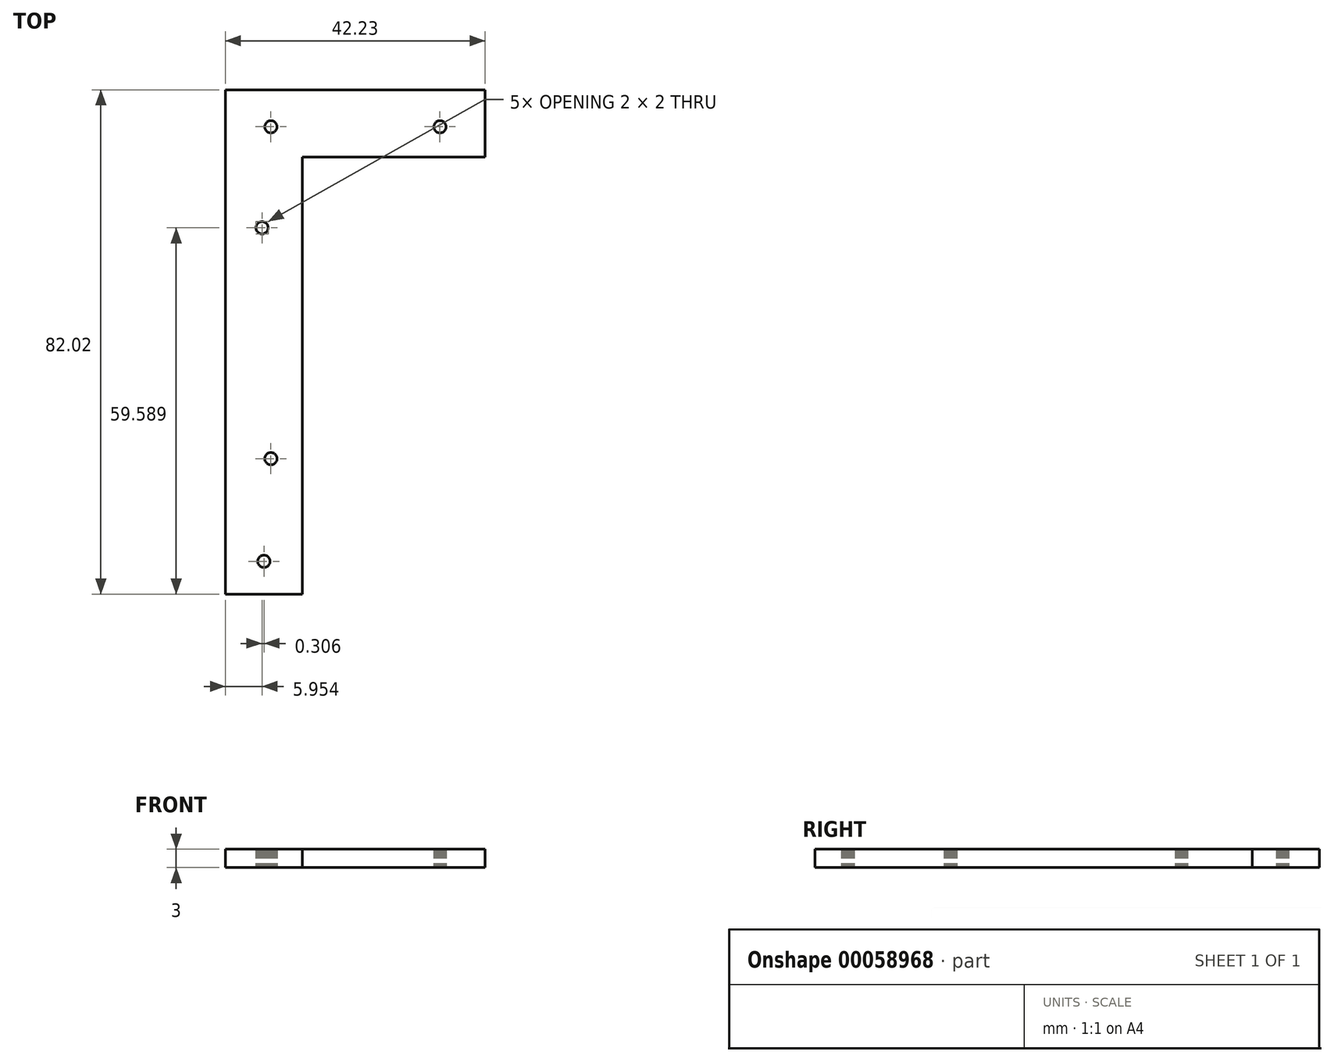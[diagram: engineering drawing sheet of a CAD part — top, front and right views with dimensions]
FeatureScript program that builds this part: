
annotation { "Feature Type Name" : "Feature", "Feature Type Description" : "" }
export const myFeature = defineFeature(function(context is Context, id is Id, definition is map)
    precondition{}
    {
        {
            var Q0;
            Q0=qCreatedBy(makeId("Top.planeOp"),FACE);
            var sketch = newSketch(context, id + "F0", { "sketchPlane" : qUnion([Q0])});
            skLineSegment(sketch, "E0", {"start": v(0.84, 33.8) * mm, "end": v(0.83, 33.92) * mm});
            skLineSegment(sketch, "E1", {"start": v(0.83, 33.92) * mm, "end": v(0.81, 34.04) * mm});
            skLineSegment(sketch, "E2", {"start": v(0.81, 34.04) * mm, "end": v(0.77, 34.16) * mm});
            skLineSegment(sketch, "E3", {"start": v(0.77, 34.16) * mm, "end": v(0.72, 34.28) * mm});
            skLineSegment(sketch, "E4", {"start": v(0.72, 34.28) * mm, "end": v(0.65, 34.38) * mm});
            skLineSegment(sketch, "E5", {"start": v(0.65, 34.38) * mm, "end": v(0.57, 34.48) * mm});
            skLineSegment(sketch, "E6", {"start": v(0.57, 34.48) * mm, "end": v(0.48, 34.57) * mm});
            skLineSegment(sketch, "E7", {"start": v(0.48, 34.57) * mm, "end": v(0.38, 34.64) * mm});
            skLineSegment(sketch, "E8", {"start": v(0.38, 34.64) * mm, "end": v(0.27, 34.7) * mm});
            skLineSegment(sketch, "E9", {"start": v(0.27, 34.7) * mm, "end": v(0.15, 34.75) * mm});
            skLineSegment(sketch, "E10", {"start": v(0.15, 34.75) * mm, "end": v(0.03, 34.78) * mm});
            skLineSegment(sketch, "E11", {"start": v(0.03, 34.78) * mm, "end": v(-0.1, 34.8) * mm});
            skLineSegment(sketch, "E12", {"start": v(-0.1, 34.8) * mm, "end": v(-0.22, 34.8) * mm});
            skLineSegment(sketch, "E13", {"start": v(-0.22, 34.8) * mm, "end": v(-0.35, 34.78) * mm});
            skLineSegment(sketch, "E14", {"start": v(-0.35, 34.78) * mm, "end": v(-0.47, 34.75) * mm});
            skLineSegment(sketch, "E15", {"start": v(-2.64, 34.75) * mm, "end": v(-2.76, 34.7) * mm});
            skLineSegment(sketch, "E16", {"start": v(-0.58, 34.7) * mm, "end": v(-0.7, 34.64) * mm});
            skLineSegment(sketch, "E17", {"start": v(-0.7, 34.64) * mm, "end": v(-0.8, 34.57) * mm});
            skLineSegment(sketch, "E18", {"start": v(-0.8, 34.57) * mm, "end": v(-0.89, 34.48) * mm});
            skLineSegment(sketch, "E19", {"start": v(-0.89, 34.48) * mm, "end": v(-0.97, 34.38) * mm});
            skLineSegment(sketch, "E20", {"start": v(-0.97, 34.38) * mm, "end": v(-1.03, 34.28) * mm});
            skLineSegment(sketch, "E21", {"start": v(-1.03, 34.28) * mm, "end": v(-1.09, 34.16) * mm});
            skLineSegment(sketch, "E22", {"start": v(-1.09, 34.16) * mm, "end": v(-1.13, 34.04) * mm});
            skLineSegment(sketch, "E23", {"start": v(-1.13, 34.04) * mm, "end": v(-1.15, 33.92) * mm});
            skLineSegment(sketch, "E24", {"start": v(-1.15, 33.92) * mm, "end": v(-1.16, 33.8) * mm});
            skLineSegment(sketch, "E25", {"start": v(-1.16, 33.8) * mm, "end": v(-1.15, 33.67) * mm});
            skLineSegment(sketch, "E26", {"start": v(-1.15, 33.67) * mm, "end": v(-1.13, 33.55) * mm});
            skLineSegment(sketch, "E27", {"start": v(-1.13, 33.55) * mm, "end": v(-1.09, 33.43) * mm});
            skLineSegment(sketch, "E28", {"start": v(-1.09, 33.43) * mm, "end": v(-1.03, 33.31) * mm});
            skLineSegment(sketch, "E29", {"start": v(-1.03, 33.31) * mm, "end": v(-0.97, 33.2) * mm});
            skLineSegment(sketch, "E30", {"start": v(-0.97, 33.2) * mm, "end": v(-0.89, 33.11) * mm});
            skLineSegment(sketch, "E31", {"start": v(-0.89, 33.11) * mm, "end": v(-0.8, 33.03) * mm});
            skLineSegment(sketch, "E32", {"start": v(-0.8, 33.03) * mm, "end": v(-0.7, 32.95) * mm});
            skLineSegment(sketch, "E33", {"start": v(-0.7, 32.95) * mm, "end": v(-0.58, 32.9) * mm});
            skLineSegment(sketch, "E34", {"start": v(-0.58, 32.9) * mm, "end": v(-0.47, 32.85) * mm});
            skLineSegment(sketch, "E35", {"start": v(-0.47, 32.85) * mm, "end": v(-0.35, 32.81) * mm});
            skLineSegment(sketch, "E36", {"start": v(-0.35, 32.81) * mm, "end": v(-0.22, 32.8) * mm});
            skLineSegment(sketch, "E37", {"start": v(-0.22, 32.8) * mm, "end": v(-0.1, 32.8) * mm});
            skLineSegment(sketch, "E38", {"start": v(-0.1, 32.8) * mm, "end": v(0.03, 32.81) * mm});
            skLineSegment(sketch, "E39", {"start": v(0.03, 32.81) * mm, "end": v(0.15, 32.85) * mm});
            skLineSegment(sketch, "E40", {"start": v(0.15, 32.85) * mm, "end": v(0.27, 32.9) * mm});
            skLineSegment(sketch, "E41", {"start": v(0.27, 32.9) * mm, "end": v(0.38, 32.95) * mm});
            skLineSegment(sketch, "E42", {"start": v(0.38, 32.95) * mm, "end": v(0.48, 33.03) * mm});
            skLineSegment(sketch, "E43", {"start": v(0.48, 33.03) * mm, "end": v(0.57, 33.11) * mm});
            skLineSegment(sketch, "E44", {"start": v(0.57, 33.11) * mm, "end": v(0.65, 33.2) * mm});
            skLineSegment(sketch, "E45", {"start": v(0.65, 33.2) * mm, "end": v(0.72, 33.31) * mm});
            skLineSegment(sketch, "E46", {"start": v(0.72, 33.31) * mm, "end": v(0.77, 33.43) * mm});
            skLineSegment(sketch, "E47", {"start": v(0.77, 33.43) * mm, "end": v(0.81, 33.55) * mm});
            skLineSegment(sketch, "E48", {"start": v(0.81, 33.55) * mm, "end": v(0.83, 33.67) * mm});
            skLineSegment(sketch, "E49", {"start": v(0.83, 33.67) * mm, "end": v(0.84, 33.8) * mm});
            skLineSegment(sketch, "E50", {"start": v(-0.29, -36.9) * mm, "end": v(-0.3, -36.78) * mm});
            skLineSegment(sketch, "E51", {"start": v(-0.3, -36.78) * mm, "end": v(-0.32, -36.66) * mm});
            skLineSegment(sketch, "E52", {"start": v(-0.32, -36.66) * mm, "end": v(-0.36, -36.54) * mm});
            skLineSegment(sketch, "E53", {"start": v(-0.36, -36.54) * mm, "end": v(-0.41, -36.42) * mm});
            skLineSegment(sketch, "E54", {"start": v(-0.41, -36.42) * mm, "end": v(-0.48, -36.32) * mm});
            skLineSegment(sketch, "E55", {"start": v(-0.48, -36.32) * mm, "end": v(-0.56, -36.22) * mm});
            skLineSegment(sketch, "E56", {"start": v(-0.56, -36.22) * mm, "end": v(-0.65, -36.14) * mm});
            skLineSegment(sketch, "E57", {"start": v(-0.65, -36.14) * mm, "end": v(-0.75, -36.06) * mm});
            skLineSegment(sketch, "E58", {"start": v(-0.75, -36.06) * mm, "end": v(-0.86, -36) * mm});
            skLineSegment(sketch, "E59", {"start": v(-0.86, -36) * mm, "end": v(-0.98, -35.95) * mm});
            skLineSegment(sketch, "E60", {"start": v(-0.98, -35.95) * mm, "end": v(-1.1, -35.92) * mm});
            skLineSegment(sketch, "E61", {"start": v(-1.1, -35.92) * mm, "end": v(-1.23, -35.9) * mm});
            skLineSegment(sketch, "E62", {"start": v(-1.23, -35.9) * mm, "end": v(-1.35, -35.9) * mm});
            skLineSegment(sketch, "E63", {"start": v(-1.35, -35.9) * mm, "end": v(-1.48, -35.92) * mm});
            skLineSegment(sketch, "E64", {"start": v(-1.48, -35.92) * mm, "end": v(-1.6, -35.95) * mm});
            skLineSegment(sketch, "E65", {"start": v(-1.6, -35.95) * mm, "end": v(-1.72, -36) * mm});
            skLineSegment(sketch, "E66", {"start": v(-1.72, -36) * mm, "end": v(-1.83, -36.06) * mm});
            skLineSegment(sketch, "E67", {"start": v(-1.83, -36.06) * mm, "end": v(-1.93, -36.14) * mm});
            skLineSegment(sketch, "E68", {"start": v(-1.93, -36.14) * mm, "end": v(-2.02, -36.22) * mm});
            skLineSegment(sketch, "E69", {"start": v(-2.02, -36.22) * mm, "end": v(-2.1, -36.32) * mm});
            skLineSegment(sketch, "E70", {"start": v(-2.1, -36.32) * mm, "end": v(-2.17, -36.42) * mm});
            skLineSegment(sketch, "E71", {"start": v(-2.17, -36.42) * mm, "end": v(-2.22, -36.54) * mm});
            skLineSegment(sketch, "E72", {"start": v(-2.22, -36.54) * mm, "end": v(-2.26, -36.66) * mm});
            skLineSegment(sketch, "E73", {"start": v(-2.26, -36.66) * mm, "end": v(-2.28, -36.78) * mm});
            skLineSegment(sketch, "E74", {"start": v(-2.28, -36.78) * mm, "end": v(-2.29, -36.9) * mm});
            skLineSegment(sketch, "E75", {"start": v(-2.29, -36.9) * mm, "end": v(-2.28, -37.03) * mm});
            skLineSegment(sketch, "E76", {"start": v(-2.28, -37.03) * mm, "end": v(-2.26, -37.15) * mm});
            skLineSegment(sketch, "E77", {"start": v(-2.26, -37.15) * mm, "end": v(-2.22, -37.27) * mm});
            skLineSegment(sketch, "E78", {"start": v(-2.22, -37.27) * mm, "end": v(-2.17, -37.39) * mm});
            skLineSegment(sketch, "E79", {"start": v(-2.17, -37.39) * mm, "end": v(-2.1, -37.5) * mm});
            skLineSegment(sketch, "E80", {"start": v(-2.1, -37.5) * mm, "end": v(-2.02, -37.6) * mm});
            skLineSegment(sketch, "E81", {"start": v(-2.02, -37.6) * mm, "end": v(-1.93, -37.68) * mm});
            skLineSegment(sketch, "E82", {"start": v(-1.93, -37.68) * mm, "end": v(-1.83, -37.75) * mm});
            skLineSegment(sketch, "E83", {"start": v(-1.83, -37.75) * mm, "end": v(-1.72, -37.81) * mm});
            skLineSegment(sketch, "E84", {"start": v(-1.72, -37.81) * mm, "end": v(-1.6, -37.86) * mm});
            skLineSegment(sketch, "E85", {"start": v(-1.6, -37.86) * mm, "end": v(-1.48, -37.89) * mm});
            skLineSegment(sketch, "E86", {"start": v(-1.48, -37.89) * mm, "end": v(-1.35, -37.9) * mm});
            skLineSegment(sketch, "E87", {"start": v(-1.35, -37.9) * mm, "end": v(-1.23, -37.9) * mm});
            skLineSegment(sketch, "E88", {"start": v(-1.23, -37.9) * mm, "end": v(-1.1, -37.89) * mm});
            skLineSegment(sketch, "E89", {"start": v(-1.1, -37.89) * mm, "end": v(-0.98, -37.86) * mm});
            skLineSegment(sketch, "E90", {"start": v(-0.98, -37.86) * mm, "end": v(-0.86, -37.81) * mm});
            skLineSegment(sketch, "E91", {"start": v(-0.86, -37.81) * mm, "end": v(-0.75, -37.75) * mm});
            skLineSegment(sketch, "E92", {"start": v(-0.75, -37.75) * mm, "end": v(-0.65, -37.68) * mm});
            skLineSegment(sketch, "E93", {"start": v(-0.65, -37.68) * mm, "end": v(-0.56, -37.6) * mm});
            skLineSegment(sketch, "E94", {"start": v(-0.56, -37.6) * mm, "end": v(-0.48, -37.5) * mm});
            skLineSegment(sketch, "E95", {"start": v(-0.48, -37.5) * mm, "end": v(-0.41, -37.39) * mm});
            skLineSegment(sketch, "E96", {"start": v(-0.41, -37.39) * mm, "end": v(-0.36, -37.27) * mm});
            skLineSegment(sketch, "E97", {"start": v(-0.36, -37.27) * mm, "end": v(-0.32, -37.15) * mm});
            skLineSegment(sketch, "E98", {"start": v(-0.32, -37.15) * mm, "end": v(-0.3, -37.03) * mm});
            skLineSegment(sketch, "E99", {"start": v(-0.3, -37.03) * mm, "end": v(-0.29, -36.9) * mm});
            skLineSegment(sketch, "E100", {"start": v(-0.6, 17.36) * mm, "end": v(-0.6, 17.48) * mm});
            skLineSegment(sketch, "E101", {"start": v(-0.6, 17.48) * mm, "end": v(-0.63, 17.6) * mm});
            skLineSegment(sketch, "E102", {"start": v(-0.63, 17.6) * mm, "end": v(-0.67, 17.73) * mm});
            skLineSegment(sketch, "E103", {"start": v(-0.67, 17.73) * mm, "end": v(-0.72, 17.84) * mm});
            skLineSegment(sketch, "E104", {"start": v(-0.72, 17.84) * mm, "end": v(-0.79, 17.95) * mm});
            skLineSegment(sketch, "E105", {"start": v(-0.79, 17.95) * mm, "end": v(-0.87, 18.04) * mm});
            skLineSegment(sketch, "E106", {"start": v(-0.87, 18.04) * mm, "end": v(-0.96, 18.13) * mm});
            skLineSegment(sketch, "E107", {"start": v(-0.96, 18.13) * mm, "end": v(-1.06, 18.2) * mm});
            skLineSegment(sketch, "E108", {"start": v(-1.06, 18.2) * mm, "end": v(-1.17, 18.26) * mm});
            skLineSegment(sketch, "E109", {"start": v(-1.17, 18.26) * mm, "end": v(-1.29, 18.3) * mm});
            skLineSegment(sketch, "E110", {"start": v(-1.29, 18.3) * mm, "end": v(-1.4, 18.34) * mm});
            skLineSegment(sketch, "E111", {"start": v(-1.4, 18.34) * mm, "end": v(-1.53, 18.36) * mm});
            skLineSegment(sketch, "E112", {"start": v(-1.53, 18.36) * mm, "end": v(-1.66, 18.36) * mm});
            skLineSegment(sketch, "E113", {"start": v(-1.66, 18.36) * mm, "end": v(-1.78, 18.34) * mm});
            skLineSegment(sketch, "E114", {"start": v(-1.78, 18.34) * mm, "end": v(-1.9, 18.3) * mm});
            skLineSegment(sketch, "E115", {"start": v(-1.9, 18.3) * mm, "end": v(-2.02, 18.26) * mm});
            skLineSegment(sketch, "E116", {"start": v(-2.02, 18.26) * mm, "end": v(-2.13, 18.2) * mm});
            skLineSegment(sketch, "E117", {"start": v(-2.13, 18.2) * mm, "end": v(-2.23, 18.13) * mm});
            skLineSegment(sketch, "E118", {"start": v(-2.23, 18.13) * mm, "end": v(-2.32, 18.04) * mm});
            skLineSegment(sketch, "E119", {"start": v(-2.32, 18.04) * mm, "end": v(-2.4, 17.95) * mm});
            skLineSegment(sketch, "E120", {"start": v(-2.4, 17.95) * mm, "end": v(-2.47, 17.84) * mm});
            skLineSegment(sketch, "E121", {"start": v(-2.47, 17.84) * mm, "end": v(-2.53, 17.73) * mm});
            skLineSegment(sketch, "E122", {"start": v(-2.53, 17.73) * mm, "end": v(-2.56, 17.6) * mm});
            skLineSegment(sketch, "E123", {"start": v(-2.56, 17.6) * mm, "end": v(-2.59, 17.48) * mm});
            skLineSegment(sketch, "E124", {"start": v(-2.59, 17.48) * mm, "end": v(-2.6, 17.36) * mm});
            skLineSegment(sketch, "E125", {"start": v(-2.6, 17.36) * mm, "end": v(-2.59, 17.23) * mm});
            skLineSegment(sketch, "E126", {"start": v(-2.59, 17.23) * mm, "end": v(-2.56, 17.11) * mm});
            skLineSegment(sketch, "E127", {"start": v(-2.56, 17.11) * mm, "end": v(-2.53, 17) * mm});
            skLineSegment(sketch, "E128", {"start": v(-2.53, 17) * mm, "end": v(-2.47, 16.88) * mm});
            skLineSegment(sketch, "E129", {"start": v(-2.47, 16.88) * mm, "end": v(-2.4, 16.77) * mm});
            skLineSegment(sketch, "E130", {"start": v(-2.4, 16.77) * mm, "end": v(-2.32, 16.67) * mm});
            skLineSegment(sketch, "E131", {"start": v(-2.32, 16.67) * mm, "end": v(-2.23, 16.59) * mm});
            skLineSegment(sketch, "E132", {"start": v(-2.23, 16.59) * mm, "end": v(-2.13, 16.51) * mm});
            skLineSegment(sketch, "E133", {"start": v(-2.13, 16.51) * mm, "end": v(-2.02, 16.45) * mm});
            skLineSegment(sketch, "E134", {"start": v(-2.02, 16.45) * mm, "end": v(-1.9, 16.4) * mm});
            skLineSegment(sketch, "E135", {"start": v(-1.9, 16.4) * mm, "end": v(-1.78, 16.38) * mm});
            skLineSegment(sketch, "E136", {"start": v(-1.78, 16.38) * mm, "end": v(-1.66, 16.36) * mm});
            skLineSegment(sketch, "E137", {"start": v(-1.66, 16.36) * mm, "end": v(-1.53, 16.36) * mm});
            skLineSegment(sketch, "E138", {"start": v(-1.53, 16.36) * mm, "end": v(-1.4, 16.38) * mm});
            skLineSegment(sketch, "E139", {"start": v(-1.4, 16.38) * mm, "end": v(-1.29, 16.4) * mm});
            skLineSegment(sketch, "E140", {"start": v(-1.29, 16.4) * mm, "end": v(-1.17, 16.45) * mm});
            skLineSegment(sketch, "E141", {"start": v(-1.17, 16.45) * mm, "end": v(-1.06, 16.51) * mm});
            skLineSegment(sketch, "E142", {"start": v(-1.06, 16.51) * mm, "end": v(-0.96, 16.59) * mm});
            skLineSegment(sketch, "E143", {"start": v(-0.96, 16.59) * mm, "end": v(-0.87, 16.67) * mm});
            skLineSegment(sketch, "E144", {"start": v(-0.87, 16.67) * mm, "end": v(-0.79, 16.77) * mm});
            skLineSegment(sketch, "E145", {"start": v(-0.79, 16.77) * mm, "end": v(-0.72, 16.88) * mm});
            skLineSegment(sketch, "E146", {"start": v(-0.72, 16.88) * mm, "end": v(-0.67, 17) * mm});
            skLineSegment(sketch, "E147", {"start": v(-0.67, 17) * mm, "end": v(-0.63, 17.11) * mm});
            skLineSegment(sketch, "E148", {"start": v(-0.63, 17.11) * mm, "end": v(-0.6, 17.23) * mm});
            skLineSegment(sketch, "E149", {"start": v(-0.6, 17.23) * mm, "end": v(-0.6, 17.36) * mm});
            skLineSegment(sketch, "E150", {"start": v(0.84, -20.2) * mm, "end": v(0.83, -20.08) * mm});
            skLineSegment(sketch, "E151", {"start": v(0.83, -20.08) * mm, "end": v(0.81, -19.96) * mm});
            skLineSegment(sketch, "E152", {"start": v(0.81, -19.96) * mm, "end": v(0.77, -19.84) * mm});
            skLineSegment(sketch, "E153", {"start": v(0.77, -19.84) * mm, "end": v(0.72, -19.72) * mm});
            skLineSegment(sketch, "E154", {"start": v(0.72, -19.72) * mm, "end": v(0.65, -19.62) * mm});
            skLineSegment(sketch, "E155", {"start": v(0.65, -19.62) * mm, "end": v(0.57, -19.52) * mm});
            skLineSegment(sketch, "E156", {"start": v(0.57, -19.52) * mm, "end": v(0.48, -19.43) * mm});
            skLineSegment(sketch, "E157", {"start": v(0.48, -19.43) * mm, "end": v(0.38, -19.36) * mm});
            skLineSegment(sketch, "E158", {"start": v(0.38, -19.36) * mm, "end": v(0.27, -19.3) * mm});
            skLineSegment(sketch, "E159", {"start": v(0.27, -19.3) * mm, "end": v(0.15, -19.25) * mm});
            skLineSegment(sketch, "E160", {"start": v(0.15, -19.25) * mm, "end": v(0.03, -19.22) * mm});
            skLineSegment(sketch, "E161", {"start": v(0.03, -19.22) * mm, "end": v(-0.1, -19.2) * mm});
            skLineSegment(sketch, "E162", {"start": v(-0.1, -19.2) * mm, "end": v(-0.22, -19.2) * mm});
            skLineSegment(sketch, "E163", {"start": v(-0.22, -19.2) * mm, "end": v(-0.35, -19.22) * mm});
            skLineSegment(sketch, "E164", {"start": v(-0.35, -19.22) * mm, "end": v(-0.47, -19.25) * mm});
            skLineSegment(sketch, "E165", {"start": v(-0.47, -19.25) * mm, "end": v(-0.58, -19.3) * mm});
            skLineSegment(sketch, "E166", {"start": v(-0.58, -19.3) * mm, "end": v(-0.7, -19.36) * mm});
            skLineSegment(sketch, "E167", {"start": v(-0.7, -19.36) * mm, "end": v(-0.8, -19.43) * mm});
            skLineSegment(sketch, "E168", {"start": v(-0.8, -19.43) * mm, "end": v(-0.89, -19.52) * mm});
            skLineSegment(sketch, "E169", {"start": v(-0.89, -19.52) * mm, "end": v(-0.97, -19.62) * mm});
            skLineSegment(sketch, "E170", {"start": v(-0.97, -19.62) * mm, "end": v(-1.03, -19.72) * mm});
            skLineSegment(sketch, "E171", {"start": v(-1.03, -19.72) * mm, "end": v(-1.09, -19.84) * mm});
            skLineSegment(sketch, "E172", {"start": v(-1.09, -19.84) * mm, "end": v(-1.13, -19.96) * mm});
            skLineSegment(sketch, "E173", {"start": v(-1.13, -19.96) * mm, "end": v(-1.15, -20.08) * mm});
            skLineSegment(sketch, "E174", {"start": v(-1.15, -20.08) * mm, "end": v(-1.16, -20.2) * mm});
            skLineSegment(sketch, "E175", {"start": v(-1.16, -20.2) * mm, "end": v(-1.15, -20.33) * mm});
            skLineSegment(sketch, "E176", {"start": v(-1.15, -20.33) * mm, "end": v(-1.13, -20.45) * mm});
            skLineSegment(sketch, "E177", {"start": v(-1.13, -20.45) * mm, "end": v(-1.09, -20.57) * mm});
            skLineSegment(sketch, "E178", {"start": v(-1.09, -20.57) * mm, "end": v(-1.03, -20.69) * mm});
            skLineSegment(sketch, "E179", {"start": v(-1.03, -20.69) * mm, "end": v(-0.97, -20.8) * mm});
            skLineSegment(sketch, "E180", {"start": v(-0.97, -20.8) * mm, "end": v(-0.89, -20.89) * mm});
            skLineSegment(sketch, "E181", {"start": v(-0.89, -20.89) * mm, "end": v(-0.8, -20.97) * mm});
            skLineSegment(sketch, "E182", {"start": v(-0.8, -20.97) * mm, "end": v(-0.7, -21.05) * mm});
            skLineSegment(sketch, "E183", {"start": v(-0.7, -21.05) * mm, "end": v(-0.58, -21.1) * mm});
            skLineSegment(sketch, "E184", {"start": v(-0.58, -21.1) * mm, "end": v(-0.47, -21.15) * mm});
            skLineSegment(sketch, "E185", {"start": v(-0.47, -21.15) * mm, "end": v(-0.35, -21.19) * mm});
            skLineSegment(sketch, "E186", {"start": v(-0.35, -21.19) * mm, "end": v(-0.22, -21.2) * mm});
            skLineSegment(sketch, "E187", {"start": v(-0.22, -21.2) * mm, "end": v(-0.1, -21.2) * mm});
            skLineSegment(sketch, "E188", {"start": v(-0.1, -21.2) * mm, "end": v(0.03, -21.19) * mm});
            skLineSegment(sketch, "E189", {"start": v(0.03, -21.19) * mm, "end": v(0.15, -21.15) * mm});
            skLineSegment(sketch, "E190", {"start": v(0.15, -21.15) * mm, "end": v(0.27, -21.1) * mm});
            skLineSegment(sketch, "E191", {"start": v(0.27, -21.1) * mm, "end": v(0.38, -21.05) * mm});
            skLineSegment(sketch, "E192", {"start": v(0.38, -21.05) * mm, "end": v(0.48, -20.97) * mm});
            skLineSegment(sketch, "E193", {"start": v(0.48, -20.97) * mm, "end": v(0.57, -20.89) * mm});
            skLineSegment(sketch, "E194", {"start": v(0.57, -20.89) * mm, "end": v(0.65, -20.8) * mm});
            skLineSegment(sketch, "E195", {"start": v(0.65, -20.8) * mm, "end": v(0.72, -20.69) * mm});
            skLineSegment(sketch, "E196", {"start": v(0.72, -20.69) * mm, "end": v(0.77, -20.57) * mm});
            skLineSegment(sketch, "E197", {"start": v(0.77, -20.57) * mm, "end": v(0.81, -20.45) * mm});
            skLineSegment(sketch, "E198", {"start": v(0.81, -20.45) * mm, "end": v(0.83, -20.33) * mm});
            skLineSegment(sketch, "E199", {"start": v(0.83, -20.33) * mm, "end": v(0.84, -20.2) * mm});
            skLineSegment(sketch, "E200", {"start": v(-0.47, 34.75) * mm, "end": v(-0.58, 34.7) * mm});
            skLineSegment(sketch, "E201", {"start": v(28.34, 33.8) * mm, "end": v(28.33, 33.92) * mm});
            skLineSegment(sketch, "E202", {"start": v(28.33, 33.92) * mm, "end": v(28.31, 34.04) * mm});
            skLineSegment(sketch, "E203", {"start": v(28.31, 34.04) * mm, "end": v(28.27, 34.16) * mm});
            skLineSegment(sketch, "E204", {"start": v(28.27, 34.16) * mm, "end": v(28.22, 34.28) * mm});
            skLineSegment(sketch, "E205", {"start": v(28.22, 34.28) * mm, "end": v(28.15, 34.38) * mm});
            skLineSegment(sketch, "E206", {"start": v(28.15, 34.38) * mm, "end": v(28.07, 34.48) * mm});
            skLineSegment(sketch, "E207", {"start": v(28.07, 34.48) * mm, "end": v(27.98, 34.57) * mm});
            skLineSegment(sketch, "E208", {"start": v(27.98, 34.57) * mm, "end": v(27.88, 34.64) * mm});
            skLineSegment(sketch, "E209", {"start": v(27.88, 34.64) * mm, "end": v(27.77, 34.7) * mm});
            skLineSegment(sketch, "E210", {"start": v(27.77, 34.7) * mm, "end": v(27.65, 34.75) * mm});
            skLineSegment(sketch, "E211", {"start": v(27.65, 34.75) * mm, "end": v(27.53, 34.78) * mm});
            skLineSegment(sketch, "E212", {"start": v(27.53, 34.78) * mm, "end": v(27.4, 34.8) * mm});
            skLineSegment(sketch, "E213", {"start": v(27.4, 34.8) * mm, "end": v(27.28, 34.8) * mm});
            skLineSegment(sketch, "E214", {"start": v(27.28, 34.8) * mm, "end": v(27.15, 34.78) * mm});
            skLineSegment(sketch, "E215", {"start": v(27.15, 34.78) * mm, "end": v(27.03, 34.75) * mm});
            skLineSegment(sketch, "E216", {"start": v(27.03, 34.75) * mm, "end": v(26.92, 34.7) * mm});
            skLineSegment(sketch, "E217", {"start": v(26.92, 34.7) * mm, "end": v(26.8, 34.64) * mm});
            skLineSegment(sketch, "E218", {"start": v(26.8, 34.64) * mm, "end": v(26.7, 34.57) * mm});
            skLineSegment(sketch, "E219", {"start": v(26.7, 34.57) * mm, "end": v(26.61, 34.48) * mm});
            skLineSegment(sketch, "E220", {"start": v(26.61, 34.48) * mm, "end": v(26.53, 34.38) * mm});
            skLineSegment(sketch, "E221", {"start": v(26.53, 34.38) * mm, "end": v(26.47, 34.28) * mm});
            skLineSegment(sketch, "E222", {"start": v(26.47, 34.28) * mm, "end": v(26.41, 34.16) * mm});
            skLineSegment(sketch, "E223", {"start": v(26.41, 34.16) * mm, "end": v(26.37, 34.04) * mm});
            skLineSegment(sketch, "E224", {"start": v(26.37, 34.04) * mm, "end": v(26.35, 33.92) * mm});
            skLineSegment(sketch, "E225", {"start": v(26.35, 33.92) * mm, "end": v(26.34, 33.8) * mm});
            skLineSegment(sketch, "E226", {"start": v(26.34, 33.8) * mm, "end": v(26.35, 33.67) * mm});
            skLineSegment(sketch, "E227", {"start": v(26.35, 33.67) * mm, "end": v(26.37, 33.55) * mm});
            skLineSegment(sketch, "E228", {"start": v(26.37, 33.55) * mm, "end": v(26.41, 33.43) * mm});
            skLineSegment(sketch, "E229", {"start": v(26.41, 33.43) * mm, "end": v(26.47, 33.31) * mm});
            skLineSegment(sketch, "E230", {"start": v(26.47, 33.31) * mm, "end": v(26.53, 33.2) * mm});
            skLineSegment(sketch, "E231", {"start": v(26.53, 33.2) * mm, "end": v(26.61, 33.11) * mm});
            skLineSegment(sketch, "E232", {"start": v(26.61, 33.11) * mm, "end": v(26.7, 33.03) * mm});
            skLineSegment(sketch, "E233", {"start": v(26.7, 33.03) * mm, "end": v(26.8, 32.95) * mm});
            skLineSegment(sketch, "E234", {"start": v(26.8, 32.95) * mm, "end": v(26.92, 32.9) * mm});
            skLineSegment(sketch, "E235", {"start": v(26.92, 32.9) * mm, "end": v(27.03, 32.85) * mm});
            skLineSegment(sketch, "E236", {"start": v(27.03, 32.85) * mm, "end": v(27.15, 32.81) * mm});
            skLineSegment(sketch, "E237", {"start": v(27.15, 32.81) * mm, "end": v(27.28, 32.8) * mm});
            skLineSegment(sketch, "E238", {"start": v(27.28, 32.8) * mm, "end": v(27.4, 32.8) * mm});
            skLineSegment(sketch, "E239", {"start": v(27.4, 32.8) * mm, "end": v(27.53, 32.81) * mm});
            skLineSegment(sketch, "E240", {"start": v(27.53, 32.81) * mm, "end": v(27.65, 32.85) * mm});
            skLineSegment(sketch, "E241", {"start": v(27.65, 32.85) * mm, "end": v(27.77, 32.9) * mm});
            skLineSegment(sketch, "E242", {"start": v(27.77, 32.9) * mm, "end": v(27.88, 32.95) * mm});
            skLineSegment(sketch, "E243", {"start": v(27.88, 32.95) * mm, "end": v(27.98, 33.03) * mm});
            skLineSegment(sketch, "E244", {"start": v(27.98, 33.03) * mm, "end": v(28.07, 33.11) * mm});
            skLineSegment(sketch, "E245", {"start": v(28.07, 33.11) * mm, "end": v(28.15, 33.2) * mm});
            skLineSegment(sketch, "E246", {"start": v(28.15, 33.2) * mm, "end": v(28.22, 33.31) * mm});
            skLineSegment(sketch, "E247", {"start": v(28.22, 33.31) * mm, "end": v(28.27, 33.43) * mm});
            skLineSegment(sketch, "E248", {"start": v(28.27, 33.43) * mm, "end": v(28.31, 33.55) * mm});
            skLineSegment(sketch, "E249", {"start": v(28.31, 33.55) * mm, "end": v(28.33, 33.67) * mm});
            skLineSegment(sketch, "E250", {"start": v(28.33, 33.67) * mm, "end": v(28.34, 33.8) * mm});
            skLineSegment(sketch, "E251", {"start": v(-2.6, 17.36) * mm, "end": v(-0.6, 17.36) * mm, "construction": true});
            skLineSegment(sketch, "E252", {"start": v(-2.29, -36.9) * mm, "end": v(-0.29, -36.9) * mm, "construction": true});
            skPoint(sketch, "E253", {"position": v(-1.29, -36.9) * mm});
            skLineSegment(sketch, "E254.bottom", {"start": v(-1.29, -42.23) * mm, "end": v(-7.55, -42.23) * mm});
            skLineSegment(sketch, "E254.top", {"start": v(-1.29, 39.79) * mm, "end": v(-7.55, 39.79) * mm});
            skLineSegment(sketch, "E254.right", {"start": v(-7.55, -42.23) * mm, "end": v(-7.55, 39.79) * mm});
            skPoint(sketch, "E255.oppositeSnap0", {"position": v(-4.42, -42.23) * mm});
            skLineSegment(sketch, "E255.bottom", {"start": v(-1.29, 39.79) * mm, "end": v(4.98, 39.79) * mm});
            skLineSegment(sketch, "E255.top", {"start": v(-1.29, -42.23) * mm, "end": v(4.98, -42.23) * mm});
            skLineSegment(sketch, "E255.right", {"start": v(4.98, 28.88) * mm, "end": v(4.98, -42.23) * mm});
            skLineSegment(sketch, "E256.bottom", {"start": v(34.68, 39.79) * mm, "end": v(4.98, 39.79) * mm});
            skLineSegment(sketch, "E256.top", {"start": v(34.68, 28.88) * mm, "end": v(4.98, 28.88) * mm});
            skLineSegment(sketch, "E256.left", {"start": v(34.68, 39.79) * mm, "end": v(34.68, 28.88) * mm});
            skSolve(sketch);
        }
        {
            var Q0;
            Q0=makeQuery(id+"F0.imprint","IMPRINT",FACE,{"disambiguationData":[TD([[makeQuery(id+"F0.imprint","IMPRINT",EDGE,{"derivedFrom":sQuery(id+"F0.wireOp",EDGE,"E50")}),-1.0]])]});
            extrude(context, id + "F1", {"entities" : qUnion([Q0]), "depth" : 3 * mm});
        }
    });
